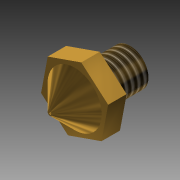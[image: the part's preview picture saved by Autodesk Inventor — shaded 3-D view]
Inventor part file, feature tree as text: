
AUTODESK INVENTOR PART (.ipt)
format: ipt  version: 2013 (Build 170138000, 138)  size: 127,488 bytes
history: native  units: mm
features: sketch x2, revolve x1, extrude x1, thread x1
ambient origin geometry x8: Origin, YZ Plane, XZ Plane, XY Plane, X Axis, Y Axis, Z Axis, Center Point
bodies: Solid1 (feature_tree)
feature tree (5):
  revolve  "Revolution1"  [1 undecoded]
  extrude  "Extrusion1"  Depth=1.0mm
  thread  "Thread1"  [1 undecoded]
  sketch  "Sketch1"  dims[d0=0.2mm d2=0.4mm]
  sketch  "Sketch2"  dims[d4=45.0deg d5=1.0mm d6=3.0mm d7=9.0mm d8=13.0mm d9=3.0mm d10=4.0mm d11=1.0mm d12=90.0deg d13=10.0mm d14=10.0mm d15=0.0mm d16=10.0mm d17=0.0mm]
note: 2 required parameter values undecoded (feature->parameter linkage not recoverable at this tier; creation-order binding heuristic only, values carry confidence <= 0.55)